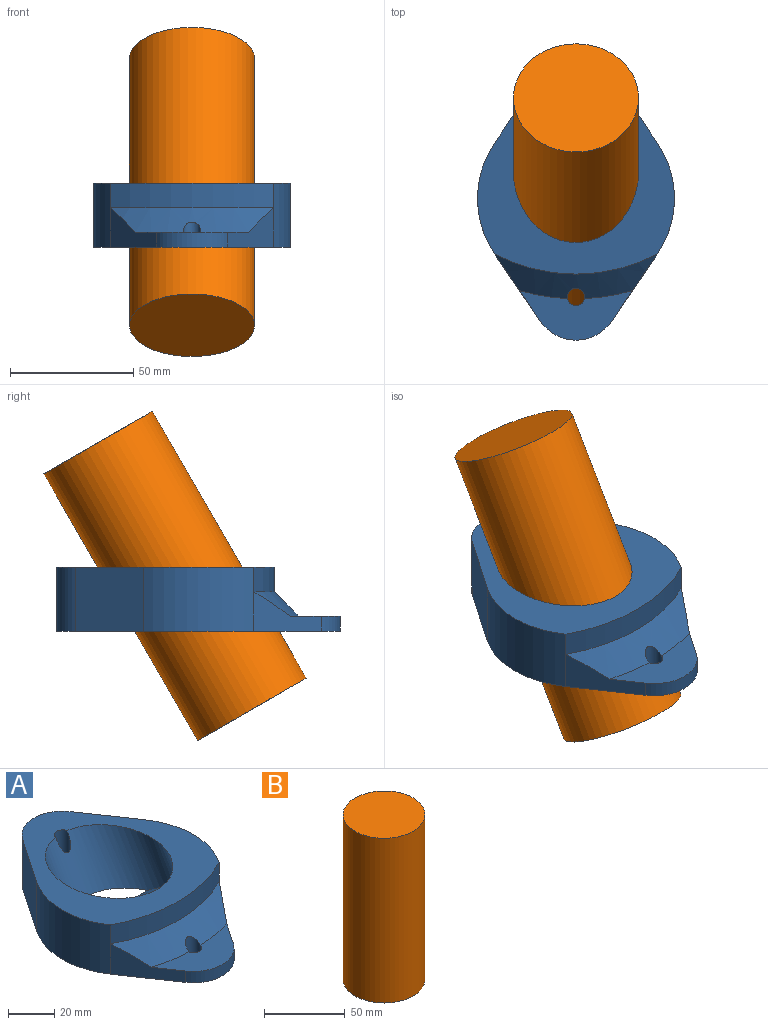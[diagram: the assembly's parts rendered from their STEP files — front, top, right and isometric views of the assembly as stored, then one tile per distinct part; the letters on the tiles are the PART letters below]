
ASSEMBLY  parts=2 mates=1
PART A: 17 faces, bbox 80x115x58.1 mm
  f0: cylinder r=3.5mm len=26mm, axis (0,0,-1), area 512.2mm2, adj f1,f13,f15
  f1: plane 115x80mm, normal (0,0,-1), area 5734.4mm2, adj f0,f2,f3,f4,f5,f6,f7,f8
  f2: plane 27.34x26mm, normal (-0.83,0.56,0), area 859.9mm2, adj f1,f3,f10,f13
  f3: cylinder r=40mm len=45mm, axis (0,0,-1), area 1242.6mm2, adj f1,f2,f4,f12,f13
  f4: plane 27.34x18.6mm, normal (-0.83,-0.56,0), area 292.9mm2, adj f1,f3,f5,f11,f16
  f5: cylinder r=17.5mm len=28.94mm, axis (0,0,-1), area 204.4mm2, adj f1,f4,f6,f11
  f6: plane 27.34x18.6mm, normal (0.83,-0.56,0), area 292.9mm2, adj f1,f5,f7,f11,f16
  f7: cylinder r=40mm len=45mm, axis (0,0,-1), area 1242.6mm2, adj f1,f6,f8,f12,f13
  f8: plane 27.34x26mm, normal (0.83,0.56,0), area 859.9mm2, adj f1,f7,f10,f13
  f9: cylinder r=3.5mm len=10.21mm, axis (0,0,-1), area 164.2mm2, adj f1,f11,f16
  f10: cylinder r=17.5mm len=28.94mm, axis (0,0,-1), area 885.8mm2, adj f1,f2,f8,f13
  f11: plane 45.9x20.12mm, normal (0,0,1), area 505.2mm2, adj f4,f5,f6,f9,f16
  f12: cylinder r=70.71mm len=66.14mm, axis (0,0,-1), area 688.3mm2, adj f3,f7,f13,f16
  f13: plane 88.21x80mm, normal (0,0,1), area 2850.2mm2, adj f0,f2,f3,f7,f8,f10,f12,f15
  f14: plane 51x32.48mm, normal (0,0.5,0.87), area 1610mm2, adj f1,f15
  f15: cylinder r=25.5mm len=63.01mm, axis (0,-0.5,-0.87), area 3368.4mm2, adj f0,f1,f13,f14
  f16: cone r=70.71mm half-angle=45deg, axis (0,0,-1), area 771.3mm2, adj f4,f6,f9,f11,f12
PART B: 3 faces, bbox 50.8x50.8x125 mm
  f0: cylinder r=25.4mm len=125mm, axis (0,0,-1), area 19949.1mm2, adj f1,f2
  f1: plane 50.8x50.8mm, normal (0,0,1), area 2026.8mm2, adj f0
  f2: plane 50.8x50.8mm, normal (0,0,-1), area 2026.8mm2, adj f0
PLACE A t=(0,40,0)mm
PLACE B rot(axis=(-0.92,0.1,0.37),32.4deg) t=(0,18.23,-31.71)mm
MATE revolute B.f0 <-> A.f15  axis (0,-0.5,-0.87) through (0,49.48,22.42)mm
